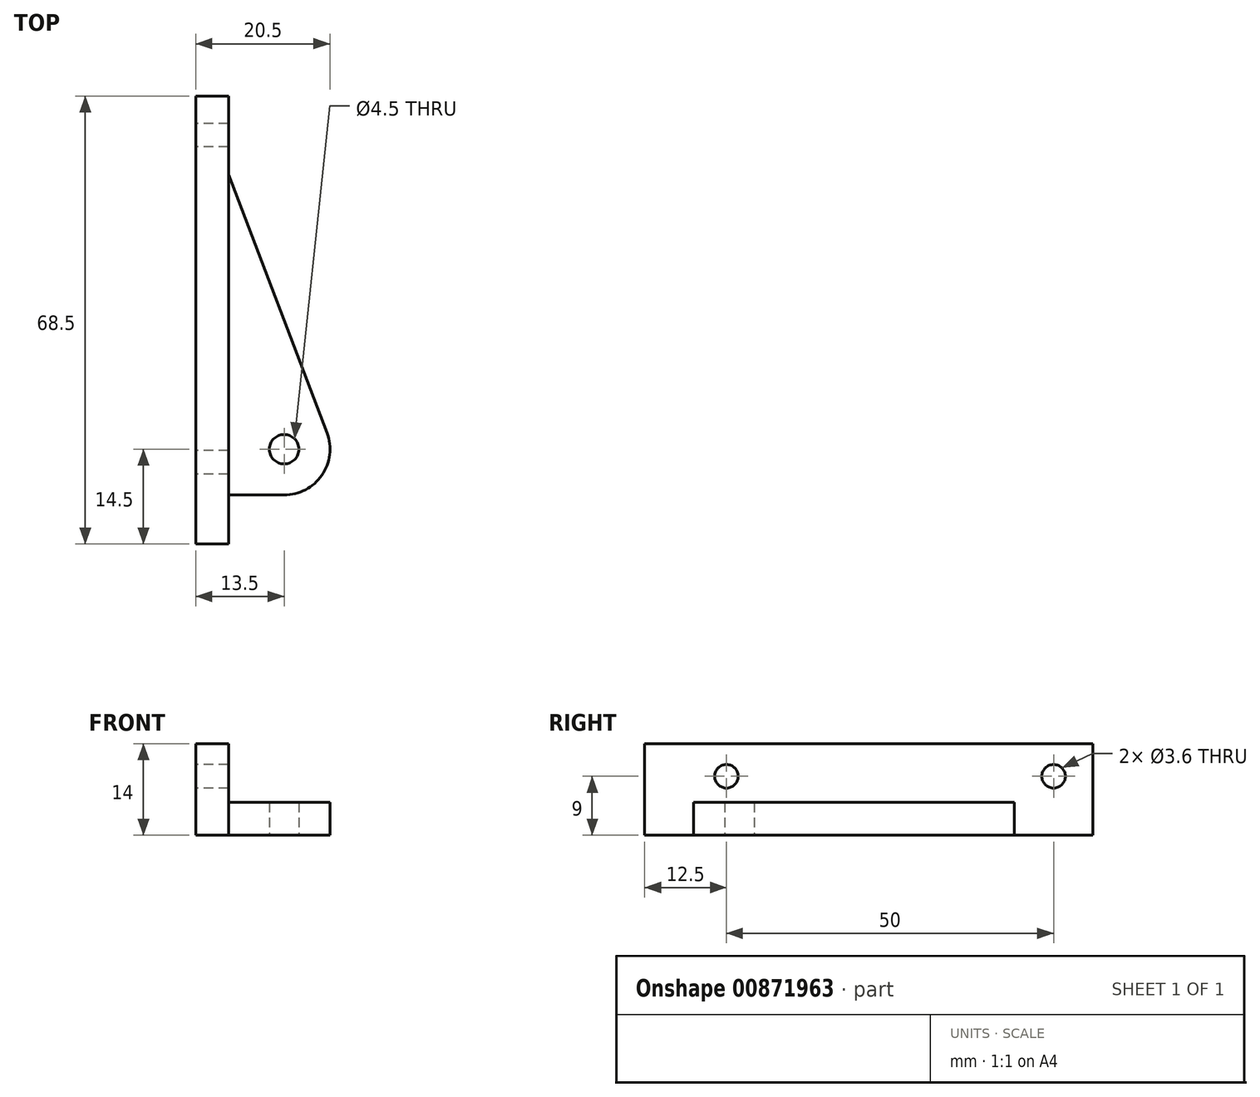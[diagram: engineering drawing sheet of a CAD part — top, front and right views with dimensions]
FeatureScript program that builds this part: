
annotation { "Feature Type Name" : "Feature", "Feature Type Description" : "" }
export const myFeature = defineFeature(function(context is Context, id is Id, definition is map)
    precondition{}
    {
        {
            var Q0;
            Q0=qCreatedBy(makeId("Top.planeOp"),FACE);
            var sketch = newSketch(context, id + "F0", { "sketchPlane" : qUnion([Q0])});
            skLineSegment(sketch, "E0.bottom", {"start": v(0, 0) * mm, "end": v(5, 0) * mm});
            skLineSegment(sketch, "E0.top", {"start": v(0, 68.5) * mm, "end": v(5, 68.5) * mm});
            skLineSegment(sketch, "E0.left", {"start": v(0, 0) * mm, "end": v(0, 68.5) * mm});
            skLineSegment(sketch, "E0.right", {"start": v(5, 0) * mm, "end": v(5, 68.5) * mm});
            skLineSegment(sketch, "E1.bottom", {"start": v(5, 21.5) * mm, "end": v(13.5, 21.5) * mm});
            skLineSegment(sketch, "E1.top", {"start": v(5, 7.5) * mm, "end": v(13.5, 7.5) * mm});
            skLineSegment(sketch, "E1.left", {"start": v(5, 21.5) * mm, "end": v(5, 7.5) * mm});
            skLineSegment(sketch, "E1.right", {"start": v(13.5, 21.5) * mm, "end": v(13.5, 7.5) * mm});
            skCircle(sketch, "E2", {"center": v(13.5, 14.5) * mm, "radius": 7 * mm});
            skCircle(sketch, "E3", {"center": v(13.5, 14.5) * mm, "radius": 2.25 * mm});
            skLineSegment(sketch, "E4", {"start": v(20.04, 17) * mm, "end": v(5, 56.5) * mm});
            skSolve(sketch);
        }
        {
            var Q0;
            {var subQ1=sQuery(id+"F0.wireOp",EDGE,"E0.bottom");Q0=makeQuery(id+"F0.imprint","IMPRINT",FACE,{"disambiguationData":[TD([[makeQuery(id+"F0.imprint","IMPRINT",EDGE,{"derivedFrom":subQ1}),1.0]])]});}
            extrude(context, id + "F1", {"entities" : qUnion([Q0]), "depth" : 14 * mm, "offsetDistance" : 25 * mm});
        }
        {
            var Q0;
            Q0=makeQuery(id+"F1.opExtrude","SWEPT_FACE",FACE,{"disambiguationData":[OSD([sQuery(id+"F0.wireOp",EDGE,"E0.left")])]});
            var sketch = newSketch(context, id + "F2", { "sketchPlane" : qUnion([Q0])});
            skCircle(sketch, "E5", {"center": v(-62.5, 9) * mm, "radius": 1.8 * mm});
            skCircle(sketch, "E6", {"center": v(-12.5, 9) * mm, "radius": 1.8 * mm});
            skSolve(sketch);
        }
        {
            var Q0;
            Q0=makeQuery(id+"F2.imprint","IMPRINT",FACE,{"disambiguationData":[TD([[makeQuery(id+"F2.imprint","IMPRINT",EDGE,{"derivedFrom":sQuery(id+"F2.wireOp",EDGE,"E5")}),1.0]])]});
            var Q1;
            Q1=makeQuery(id+"F2.imprint","IMPRINT",FACE,{"disambiguationData":[TD([[makeQuery(id+"F2.imprint","IMPRINT",EDGE,{"derivedFrom":sQuery(id+"F2.wireOp",EDGE,"E6")}),1.0]])]});
            extrude(context, id + "F3", {"entities" : qUnion([Q0, Q1]), "operationType" : NewBodyOperationType.REMOVE, "oppositeDirection" : true, "depth" : 25 * mm, "offsetDistance" : 25 * mm});
        }
        {
            var Q0;
            {var subQ0=sQuery(id+"F0.wireOp",EDGE,"E1.bottom");Q0=makeQuery(id+"F0.imprint","IMPRINT",FACE,{"disambiguationData":[TD([[makeQuery(id+"F0.imprint","IMPRINT",EDGE,{"derivedFrom":subQ0}),1.0]])]});}
            var Q1;
            {var subQ0=sQuery(id+"F0.wireOp",EDGE,"E1.bottom");Q1=makeQuery(id+"F0.imprint","IMPRINT",FACE,{"disambiguationData":[TD([[makeQuery(id+"F0.imprint","IMPRINT",EDGE,{"derivedFrom":subQ0}),-1.0]])]});}
            var Q2;
            {var subQ1=sQuery(id+"F0.wireOp",EDGE,"E1.right");var subQ3=sQuery(id+"F0.wireOp",EDGE,"E3");var subQ4=makeQuery(id+"F0.imprint","INTERSECT",VERTEX,{"disambiguationData":[OD(0.0)],"derivedFrom":[subQ1,subQ3]});Q2=makeQuery(id+"F0.imprint","IMPRINT",FACE,{"disambiguationData":[TD([[makeQuery(id+"F0.imprint","IMPRINT",EDGE,{"disambiguationData":[TD([[subQ4,-1.0]])],"derivedFrom":subQ3}),-1.0]])]});}
            var Q3;
            {var subQ1=sQuery(id+"F0.wireOp",EDGE,"E1.right");var subQ5=sQuery(id+"F0.wireOp",EDGE,"E3");var subQ7=makeQuery(id+"F0.imprint","INTERSECT",VERTEX,{"disambiguationData":[OD(0.0)],"derivedFrom":[subQ1,subQ5]});Q3=makeQuery(id+"F0.imprint","IMPRINT",FACE,{"disambiguationData":[TD([[makeQuery(id+"F0.imprint","IMPRINT",EDGE,{"disambiguationData":[TD([[subQ7,1.0]])],"derivedFrom":subQ5}),-1.0]])]});}
            extrude(context, id + "F4", {"entities" : qUnion([Q0, Q1, Q2, Q3]), "operationType" : NewBodyOperationType.ADD, "depth" : 5 * mm, "offsetDistance" : 25 * mm});
        }
    });
